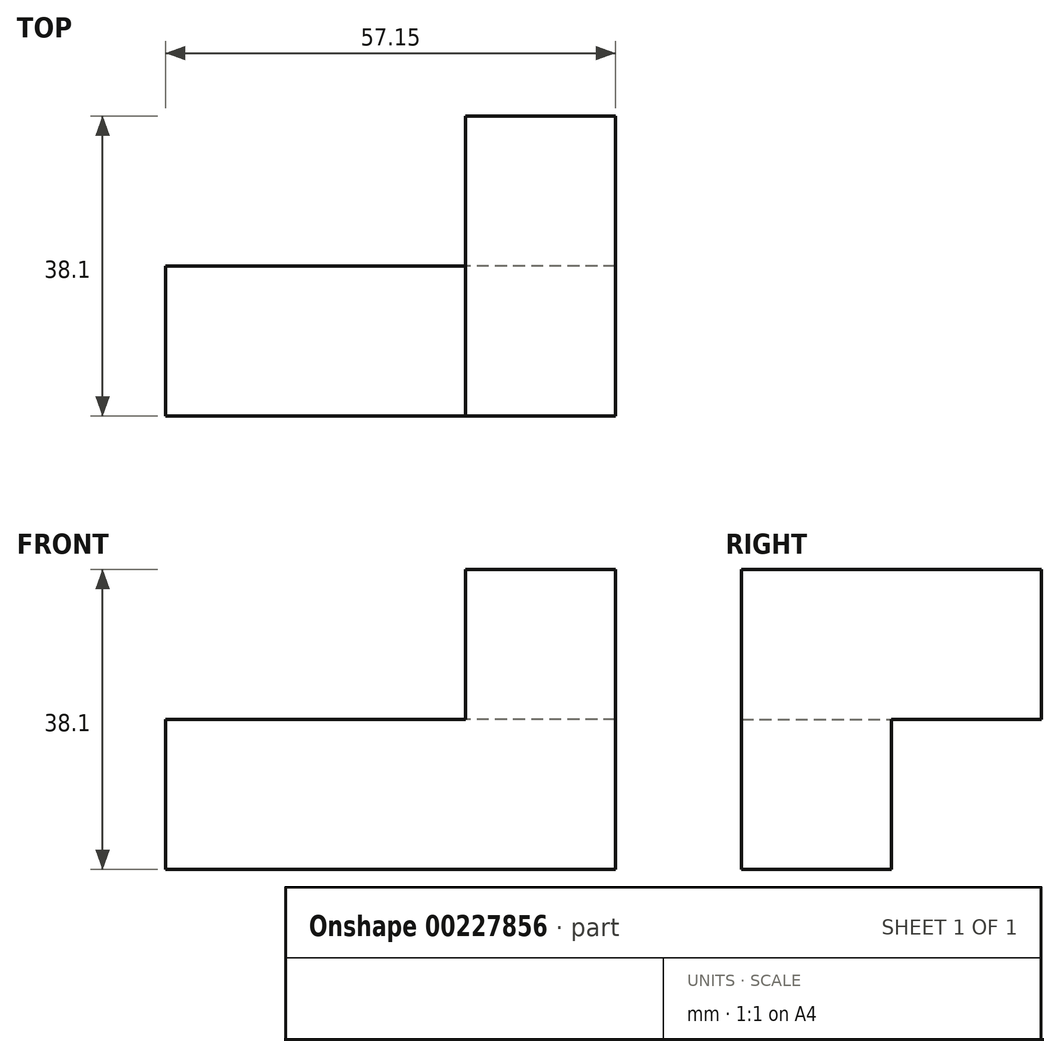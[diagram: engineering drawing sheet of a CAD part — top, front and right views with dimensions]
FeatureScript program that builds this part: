
annotation { "Feature Type Name" : "Feature", "Feature Type Description" : "" }
export const myFeature = defineFeature(function(context is Context, id is Id, definition is map)
    precondition{}
    {
        {
            var Q0;
            Q0=qCreatedBy(makeId("Top.planeOp"),FACE);
            var sketch = newSketch(context, id + "F0", { "sketchPlane" : qUnion([Q0])});
            skLineSegment(sketch, "E0.bottom", {"start": v(-57.15, 36.7) * mm, "end": v(0, 36.7) * mm});
            skLineSegment(sketch, "E0.top", {"start": v(-57.15, 17.64) * mm, "end": v(0, 17.64) * mm});
            skLineSegment(sketch, "E0.left", {"start": v(-57.15, 36.7) * mm, "end": v(-57.15, 17.64) * mm});
            skLineSegment(sketch, "E0.right", {"start": v(0, 36.7) * mm, "end": v(0, 17.64) * mm});
            skLineSegment(sketch, "E1", {"start": v(0, 17.64) * mm, "end": v(-19.05, 17.64) * mm});
            skLineSegment(sketch, "E2", {"start": v(-19.05, 36.7) * mm, "end": v(-19.05, 17.64) * mm});
            skSolve(sketch);
        }
        {
            var Q0;
            Q0=makeQuery(id+"F0.imprint","IMPRINT",FACE,{"disambiguationData":[TD([[makeQuery(id+"F0.imprint","IMPRINT",EDGE,{"derivedFrom":sQuery(id+"F0.wireOp",EDGE,"E0.bottom")}),-1.0]])]});
            extrude(context, id + "F1", {"entities" : qUnion([Q0]), "depth" : 19.05 * mm});
        }
        {
            var Q0;
            {var subQ0=sQuery(id+"F0.wireOp",EDGE,"E0.right");Q0=makeQuery(id+"F0.imprint","IMPRINT",FACE,{"disambiguationData":[TD([[makeQuery(id+"F0.imprint","IMPRINT",EDGE,{"derivedFrom":subQ0}),-1.0]])]});}
            extrude(context, id + "F2", {"entities" : qUnion([Q0]), "operationType" : NewBodyOperationType.ADD, "depth" : 38.1 * mm});
        }
        {
            var Q0;
            {var subQ0=sQuery(id+"F0.wireOp",EDGE,"E0.bottom");Q0=makeQuery(id+"F2.boolean.opBoolean","MERGE",FACE,{"derivedFrom":[makeQuery(id+"F1.opExtrude","SWEPT_FACE",FACE,{"disambiguationData":[OSD([subQ0])]}),makeQuery(id+"F2.opExtrude","SWEPT_FACE",FACE,{"disambiguationData":[OSD([subQ0])]})]});}
            var sketch = newSketch(context, id + "F3", { "sketchPlane" : qUnion([Q0])});
            skLineSegment(sketch, "E3", {"start": v(0, 19.05) * mm, "end": v(19.05, 19.05) * mm});
            skSolve(sketch);
        }
        {
            var Q0;
            {var subQ0=sQuery(id+"F0.wireOp",EDGE,"E0.bottom");Q0=makeQuery(id+"F3.imprint","IMPRINT",FACE,{"disambiguationData":[TD([[makeQuery(id+"F3.imprint","IMPRINT",EDGE,{"derivedFrom":makeQuery(id+"F2.opExtrude","CAP_EDGE",EDGE,{"disambiguationData":[OSD([subQ0])],"isStart":false})}),1.0]])]});}
            var sketch = newSketch(context, id + "F4", { "sketchPlane" : qUnion([Q0])});
            skSolve(sketch);
        }
        {
            var Q0;
            {var subQ0=sQuery(id+"F3.wireOp",EDGE,"E3");Q0=makeQuery(id+"F4.imprint","IMPRINT",FACE,{"disambiguationData":[TD([[makeQuery(id+"F4.imprint","IMPRINT",EDGE,{"derivedFrom":makeQuery(id+"F3.imprint","IMPRINT",EDGE,{"derivedFrom":subQ0})}),1.0]])]});}
            extrude(context, id + "F5", {"entities" : qUnion([Q0]), "operationType" : NewBodyOperationType.ADD, "depth" : 19.05 * mm});
        }
    });
